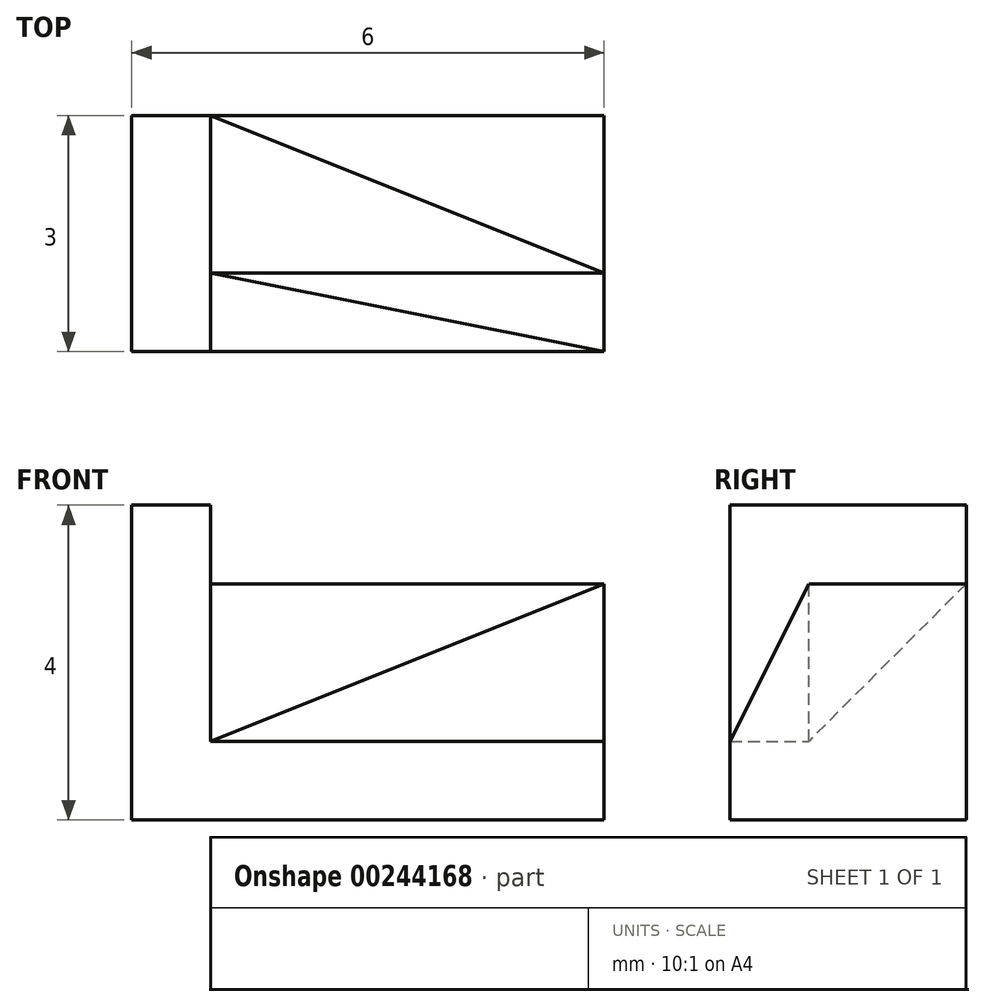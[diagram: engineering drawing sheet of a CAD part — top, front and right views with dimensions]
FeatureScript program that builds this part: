
annotation { "Feature Type Name" : "Feature", "Feature Type Description" : "" }
export const myFeature = defineFeature(function(context is Context, id is Id, definition is map)
    precondition{}
    {
        {
            var Q0;
            Q0=qCreatedBy(makeId("Top.planeOp"),FACE);
            var sketch = newSketch(context, id + "F0", { "sketchPlane" : qUnion([Q0])});
            skLineSegment(sketch, "E0.bottom", {"start": v(0, 0) * mm, "end": v(5, 0) * mm});
            skLineSegment(sketch, "E0.top", {"start": v(0, 3) * mm, "end": v(5, 3) * mm});
            skLineSegment(sketch, "E0.left", {"start": v(0, 0) * mm, "end": v(0, 3) * mm});
            skLineSegment(sketch, "E0.right", {"start": v(5, 0) * mm, "end": v(5, 3) * mm});
            skSolve(sketch);
        }
        {
            var Q0;
            Q0 = qSketchRegion(id + "F0", true);
            extrude(context, id + "F1", {"entities" : qUnion([Q0]), "depth" : 3 * mm});
        }
        {
            var Q0;
            Q0=makeQuery(id+"F1.opExtrude","CAP_FACE",FACE,{"disambiguationData":[OSD([sQuery(id+"F0.wireOp",EDGE,"E0.bottom"),sQuery(id+"F0.wireOp",EDGE,"E0.top"),sQuery(id+"F0.wireOp",EDGE,"E0.left"),sQuery(id+"F0.wireOp",EDGE,"E0.right")])],"isStart":false});
            var sketch = newSketch(context, id + "F2", { "sketchPlane" : qUnion([Q0])});
            skLineSegment(sketch, "E1", {"start": v(0, 0) * mm, "end": v(5, 0) * mm});
            skLineSegment(sketch, "E2", {"start": v(5, 0) * mm, "end": v(0, 1) * mm});
            skLineSegment(sketch, "E3", {"start": v(0, 1) * mm, "end": v(0, 0) * mm});
            skSolve(sketch);
        }
        {
            var Q0;
            Q0 = qSketchRegion(id + "F2", true);
            extrude(context, id + "F3", {"entities" : qUnion([Q0]), "operationType" : NewBodyOperationType.REMOVE, "oppositeDirection" : true, "depth" : 2 * mm});
        }
        {
            var Q0;
            Q0=makeQuery(id+"F1.opExtrude","SWEPT_FACE",FACE,{"disambiguationData":[OSD([sQuery(id+"F0.wireOp",EDGE,"E0.right")])]});
            var sketch = newSketch(context, id + "F4", { "sketchPlane" : qUnion([Q0])});
            skLineSegment(sketch, "E4", {"start": v(0, 0) * mm, "end": v(1, 0) * mm, "construction": true});
            skLineSegment(sketch, "E5", {"start": v(1, 0) * mm, "end": v(1, 3) * mm, "construction": true});
            skSolve(sketch);
        }
        {
            var Q0;
            Q0=makeQuery(id+"F3.boolean.opBoolean","COPY",VERTEX,{"derivedFrom":makeQuery(id+"F3.opExtrude","CAP_VERTEX",VERTEX,{"disambiguationData":[OSD([sQuery(id+"F0.wireOp",EDGE,"E0.left"),sQuery(id+"F2.wireOp",EDGE,"E2"),sQuery(id+"F2.wireOp",EDGE,"E3")])],"isStart":false})});
            var Q1;
            Q1=makeQuery(id+"F3.boolean.opBoolean","COPY",VERTEX,{"derivedFrom":makeQuery(id+"F3.opExtrude","CAP_VERTEX",VERTEX,{"disambiguationData":[OSD([sQuery(id+"F0.wireOp",EDGE,"E0.right"),sQuery(id+"F2.wireOp",EDGE,"E1"),sQuery(id+"F2.wireOp",EDGE,"E2")])],"isStart":false})});
            var Q2;
            Q2=sQuery(id+"F4.wireOp",VERTEX,"E5.end");
            cPlane(context, id + "F5", {"entities" : qUnion([Q0, Q1, Q2]), "cplaneType" : CPlaneType.THREE_POINT, "offset" : 25 * mm, "width" : 150 * mm, "height" : 150 * mm});
        }
        {
            var Q0;
            Q0=qCreatedBy(id+"F5.planeOp",FACE);
            var sketch = newSketch(context, id + "F6", { "sketchPlane" : qUnion([Q0])});
            skPoint(sketch, "E6.0", {"position": v(0.08, 1.34) * mm});
            skPoint(sketch, "E6.1", {"position": v(-5, 3.13) * mm});
            skPoint(sketch, "E6.2", {"position": v(-5, 0.9) * mm});
            skLineSegment(sketch, "E7", {"start": v(0.08, 1.34) * mm, "end": v(-5, 3.13) * mm});
            skLineSegment(sketch, "E8", {"start": v(0.08, 1.34) * mm, "end": v(-5, 0.9) * mm});
            skLineSegment(sketch, "E9", {"start": v(-5, 3.13) * mm, "end": v(-5.73, 3.13) * mm});
            skLineSegment(sketch, "E10", {"start": v(-5, 0.9) * mm, "end": v(-5.73, 0.9) * mm});
            skLineSegment(sketch, "E11", {"start": v(-5.73, 0.9) * mm, "end": v(-5.73, 3.13) * mm});
            skSolve(sketch);
        }
        {
            var Q0;
            Q0 = qSketchRegion(id + "F6", true);
            extrude(context, id + "F7", {"entities" : qUnion([Q0]), "operationType" : NewBodyOperationType.REMOVE, "oppositeDirection" : true, "depth" : 25 * mm});
        }
        {
            var Q0;
            Q0=makeQuery(id+"F7.boolean.opBoolean","MERGE",VERTEX,{"derivedFrom":[makeQuery(id+"F3.boolean.opBoolean","COPY",VERTEX,{"derivedFrom":makeQuery(id+"F3.opExtrude","CAP_VERTEX",VERTEX,{"disambiguationData":[OSD([sQuery(id+"F0.wireOp",EDGE,"E0.left"),sQuery(id+"F2.wireOp",EDGE,"E2"),sQuery(id+"F2.wireOp",EDGE,"E3")])],"isStart":false})}),makeQuery(id+"F7.opExtrude","CAP_VERTEX",VERTEX,{"disambiguationData":[OSD([sQuery(id+"F6.wireOp",EDGE,"E7"),sQuery(id+"F6.wireOp",EDGE,"E8")])],"isStart":true})]});
            var Q1;
            Q1=sQuery(id+"F4.wireOp",VERTEX,"E5.end");
            var Q2;
            Q2=makeQuery(id+"F1.opExtrude","CAP_VERTEX",VERTEX,{"disambiguationData":[OSD([sQuery(id+"F0.wireOp",EDGE,"E0.top"),sQuery(id+"F0.wireOp",EDGE,"E0.left")])],"isStart":false});
            cPlane(context, id + "F8", {"entities" : qUnion([Q0, Q1, Q2]), "cplaneType" : CPlaneType.THREE_POINT, "offset" : 25 * mm, "width" : 150 * mm, "height" : 150 * mm});
        }
        {
            var Q0;
            Q0=qCreatedBy(id+"F8.planeOp",FACE);
            var sketch = newSketch(context, id + "F9", { "sketchPlane" : qUnion([Q0])});
            skPoint(sketch, "E12.0", {"position": v(0, 1.41) * mm});
            skPoint(sketch, "E12.1", {"position": v(0, 4.24) * mm});
            skPoint(sketch, "E12.2", {"position": v(-5.2, 2.83) * mm});
            skLineSegment(sketch, "E13", {"start": v(-5.2, 2.83) * mm, "end": v(0, 4.24) * mm});
            skLineSegment(sketch, "E14", {"start": v(0, 4.24) * mm, "end": v(0, 1.41) * mm});
            skLineSegment(sketch, "E15", {"start": v(-5.2, 2.83) * mm, "end": v(-5.48, 1.8) * mm});
            skLineSegment(sketch, "E16", {"start": v(-5.48, 1.8) * mm, "end": v(0, 1.41) * mm});
            skSolve(sketch);
        }
        {
            var Q0;
            Q0 = qSketchRegion(id + "F9", true);
            extrude(context, id + "F10", {"entities" : qUnion([Q0]), "operationType" : NewBodyOperationType.REMOVE, "oppositeDirection" : true, "depth" : 25 * mm});
        }
        {
            var Q0;
            Q0=qCreatedBy(makeId("Top.planeOp"),FACE);
            var sketch = newSketch(context, id + "F11", { "sketchPlane" : qUnion([Q0])});
            skLineSegment(sketch, "E17.bottom", {"start": v(0, 0) * mm, "end": v(-1, 0) * mm});
            skLineSegment(sketch, "E17.top", {"start": v(0, 3) * mm, "end": v(-1, 3) * mm});
            skLineSegment(sketch, "E17.left", {"start": v(0, 0) * mm, "end": v(0, 3) * mm});
            skLineSegment(sketch, "E17.right", {"start": v(-1, 0) * mm, "end": v(-1, 3) * mm});
            skSolve(sketch);
        }
        {
            var Q0;
            Q0 = qSketchRegion(id + "F11", true);
            extrude(context, id + "F12", {"entities" : qUnion([Q0]), "operationType" : NewBodyOperationType.ADD, "depth" : 4 * mm});
        }
    });
